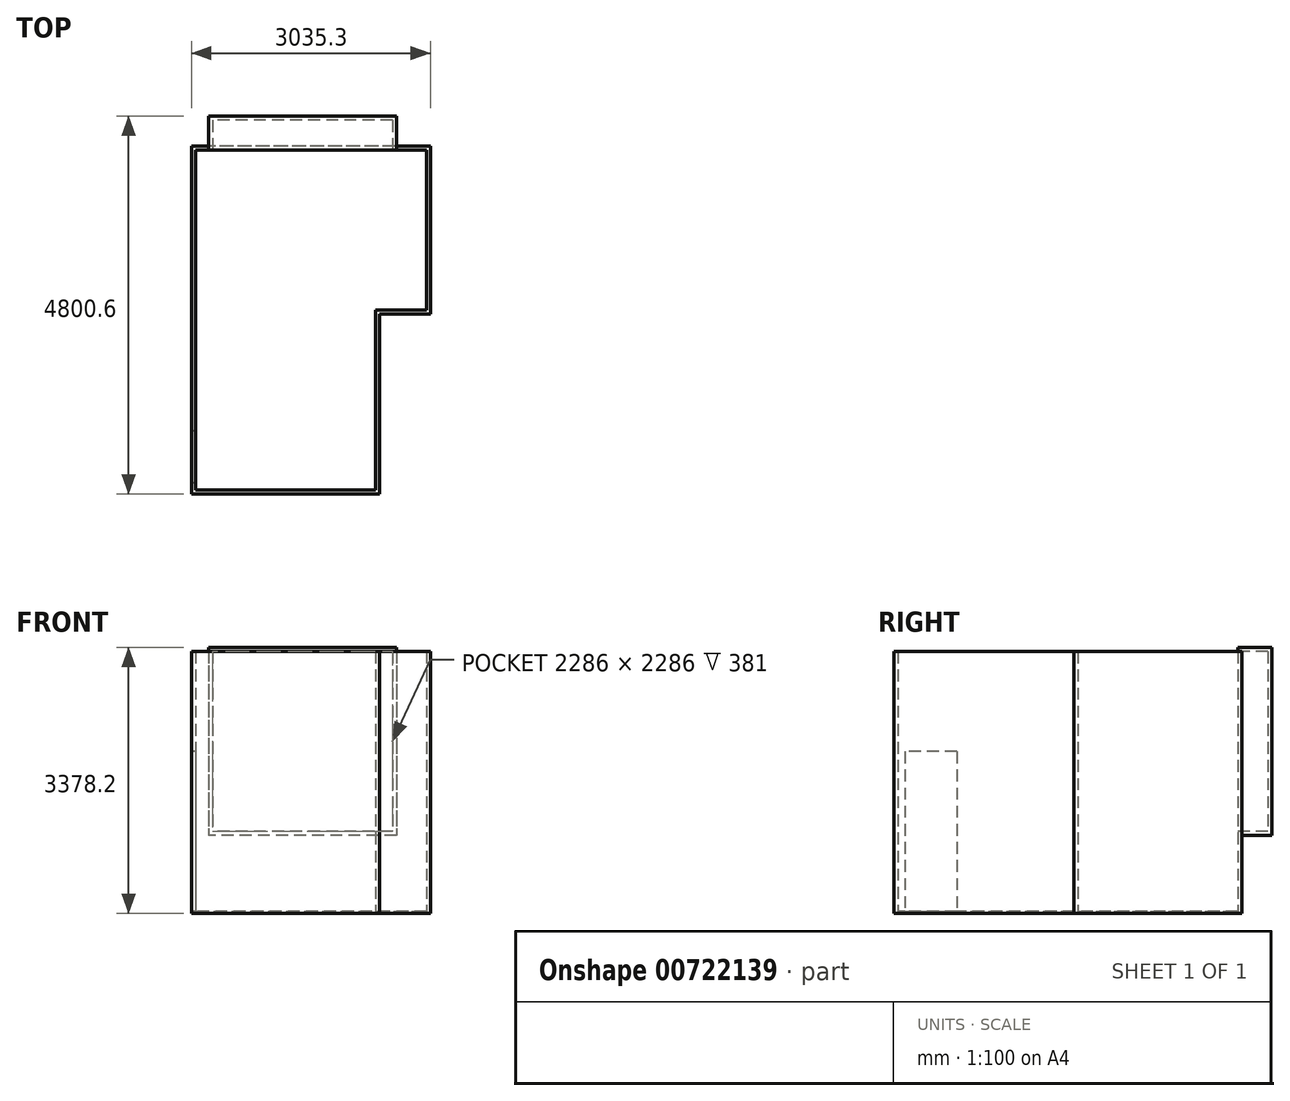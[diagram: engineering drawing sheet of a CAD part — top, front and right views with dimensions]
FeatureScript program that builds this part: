
annotation { "Feature Type Name" : "Feature", "Feature Type Description" : "" }
export const myFeature = defineFeature(function(context is Context, id is Id, definition is map)
    precondition{}
    {
        {
            var Q0;
            Q0=qCreatedBy(makeId("Top.planeOp"),FACE);
            var sketch = newSketch(context, id + "F0", { "sketchPlane" : qUnion([Q0])});
            skLineSegment(sketch, "E0", {"start": v(50.8, 4368.8) * mm, "end": v(50.8, 50.8) * mm});
            skLineSegment(sketch, "E1", {"start": v(50.8, 50.8) * mm, "end": v(2336.8, 50.8) * mm});
            skLineSegment(sketch, "E2", {"start": v(2336.8, 50.8) * mm, "end": v(2336.8, 2336.8) * mm});
            skLineSegment(sketch, "E3", {"start": v(2336.8, 2336.8) * mm, "end": v(2984.5, 2336.8) * mm});
            skLineSegment(sketch, "E4", {"start": v(2984.5, 2336.8) * mm, "end": v(2984.5, 4368.8) * mm});
            skLineSegment(sketch, "E5", {"start": v(2984.5, 4368.8) * mm, "end": v(50.8, 4368.8) * mm});
            skLineSegment(sketch, "E6", {"start": v(0, 4419.6) * mm, "end": v(0, 0) * mm});
            skLineSegment(sketch, "E7", {"start": v(0, 0) * mm, "end": v(2387.6, 0) * mm});
            skLineSegment(sketch, "E8", {"start": v(2387.6, 0) * mm, "end": v(2387.6, 2286) * mm});
            skLineSegment(sketch, "E9", {"start": v(2387.6, 2286) * mm, "end": v(3035.3, 2286) * mm});
            skLineSegment(sketch, "E10", {"start": v(3035.3, 2286) * mm, "end": v(3035.3, 4419.6) * mm});
            skLineSegment(sketch, "E11", {"start": v(3035.3, 4419.6) * mm, "end": v(0, 4419.6) * mm});
            skLineSegment(sketch, "E12", {"start": v(1193.8, 50.8) * mm, "end": v(1193.8, 0) * mm, "construction": true});
            skLineSegment(sketch, "E13", {"start": v(1517.65, 4368.8) * mm, "end": v(1517.65, 4419.6) * mm, "construction": true});
            skLineSegment(sketch, "E14", {"start": v(2984.5, 3352.8) * mm, "end": v(3035.3, 3352.8) * mm, "construction": true});
            skLineSegment(sketch, "E15", {"start": v(2336.8, 2286) * mm, "end": v(2387.6, 2286) * mm, "construction": true});
            skLineSegment(sketch, "E16", {"start": v(2362.2, 2336.8) * mm, "end": v(2362.2, 2286) * mm, "construction": true});
            skSolve(sketch);
        }
        {
            var Q0;
            Q0=makeQuery(id+"F0.imprint","IMPRINT",FACE,{"disambiguationData":[TD([[makeQuery(id+"F0.imprint","IMPRINT",EDGE,{"derivedFrom":sQuery(id+"F0.wireOp",EDGE,"E0")}),-1.0]])]});
            var sketch = newSketch(context, id + "F1", { "sketchPlane" : qUnion([Q0])});
            skLineSegment(sketch, "E17.top", {"start": v(0, 4419.6) * mm, "end": v(3035.3, 4419.6) * mm, "construction": true});
            skLineSegment(sketch, "E17.left", {"start": v(0, 0) * mm, "end": v(0, 4419.6) * mm});
            skLineSegment(sketch, "E18.bottom", {"start": v(0, 0) * mm, "end": v(2387.6, 0) * mm});
            skLineSegment(sketch, "E18.top", {"start": v(0, 4419.6) * mm, "end": v(3035.3, 4419.6) * mm});
            skLineSegment(sketch, "E19", {"start": v(3035.3, 4419.6) * mm, "end": v(3035.3, 2286) * mm});
            skLineSegment(sketch, "E20", {"start": v(3035.3, 2286) * mm, "end": v(2387.6, 2286) * mm});
            skLineSegment(sketch, "E21", {"start": v(2387.6, 2286) * mm, "end": v(2387.6, 0) * mm});
            skSolve(sketch);
        }
        {
            var Q0;
            Q0 = qSketchRegion(id + "F0", true);
            extrude(context, id + "F2", {"entities" : qUnion([Q0]), "depth" : 3302 * mm, "offsetDistance" : 25.4 * mm});
        }
        {
            var Q0;
            Q0 = qSketchRegion(id + "F1", true);
            extrude(context, id + "F3", {"entities" : qUnion([Q0]), "operationType" : NewBodyOperationType.ADD, "oppositeDirection" : true, "depth" : 25.4 * mm, "offsetDistance" : 25.4 * mm});
        }
        {
            var Q0;
            Q0=makeQuery(id+"F2.opExtrude","SWEPT_FACE",FACE,{"disambiguationData":[OSD([sQuery(id+"F0.wireOp",EDGE,"E6")])]});
            var sketch = newSketch(context, id + "F4", { "sketchPlane" : qUnion([Q0])});
            skLineSegment(sketch, "E22.bottom", {"start": v(-800.1, 2032) * mm, "end": v(-139.7, 2032) * mm});
            skLineSegment(sketch, "E22.top", {"start": v(-800.1, 0) * mm, "end": v(-139.7, 0) * mm});
            skLineSegment(sketch, "E22.left", {"start": v(-800.1, 2032) * mm, "end": v(-800.1, 0) * mm});
            skLineSegment(sketch, "E22.right", {"start": v(-139.7, 2032) * mm, "end": v(-139.7, 0) * mm});
            skLineSegment(sketch, "E23", {"start": v(-139.7, 2032) * mm, "end": v(0, 2032) * mm, "construction": true});
            skSolve(sketch);
        }
        {
            var Q0;
            Q0 = qSketchRegion(id + "F4", true);
            extrude(context, id + "F5", {"entities" : qUnion([Q0]), "operationType" : NewBodyOperationType.REMOVE, "endBound" : BoundingType.UP_TO_NEXT, "oppositeDirection" : true, "depth" : 25.4 * mm, "offsetDistance" : 25.4 * mm});
        }
        {
            var Q0;
            Q0=makeQuery(id+"F2.opExtrude","SWEPT_FACE",FACE,{"disambiguationData":[OSD([sQuery(id+"F0.wireOp",EDGE,"E5")])]});
            var sketch = newSketch(context, id + "F6", { "sketchPlane" : qUnion([Q0])});
            skLineSegment(sketch, "E24", {"start": v(1409.7, 0) * mm, "end": v(1409.7, 1016) * mm, "construction": true});
            skLineSegment(sketch, "E25.bottom", {"start": v(2552.7, 3302) * mm, "end": v(266.7, 3302) * mm, "construction": true});
            skLineSegment(sketch, "E25.top", {"start": v(2552.7, 1016) * mm, "end": v(266.7, 1016) * mm, "construction": true});
            skLineSegment(sketch, "E25.left", {"start": v(2552.7, 3302) * mm, "end": v(2552.7, 1016) * mm, "construction": true});
            skLineSegment(sketch, "E25.right", {"start": v(266.7, 3302) * mm, "end": v(266.7, 1016) * mm, "construction": true});
            skLineSegment(sketch, "E26", {"start": v(50.8, 2159) * mm, "end": v(266.7, 2159) * mm});
            skLineSegment(sketch, "E27.bottom", {"start": v(2603.5, 3352.8) * mm, "end": v(215.9, 3352.8) * mm});
            skLineSegment(sketch, "E27.top", {"start": v(2603.5, 965.2) * mm, "end": v(215.9, 965.2) * mm});
            skLineSegment(sketch, "E27.left", {"start": v(215.9, 3352.8) * mm, "end": v(215.9, 965.2) * mm});
            skLineSegment(sketch, "E27.right", {"start": v(2603.5, 3352.8) * mm, "end": v(2603.5, 965.2) * mm});
            skLineSegment(sketch, "E28", {"start": v(1409.7, 965.2) * mm, "end": v(1409.7, 1016) * mm, "construction": true});
            skLineSegment(sketch, "E29", {"start": v(2552.7, 2159) * mm, "end": v(2603.5, 2159) * mm, "construction": true});
            skSolve(sketch);
        }
        {
            var Q0;
            Q0 = qSketchRegion(id + "F6", true);
            extrude(context, id + "F7", {"entities" : qUnion([Q0]), "operationType" : NewBodyOperationType.ADD, "oppositeDirection" : true, "depth" : 431.8 * mm, "offsetDistance" : 25.4 * mm});
        }
        {
            var Q0;
            Q0=makeQuery(id+"F7.boolean.opBoolean","MERGE",FACE,{"derivedFrom":[makeQuery(id+"F2.opExtrude","SWEPT_FACE",FACE,{"disambiguationData":[OSD([sQuery(id+"F0.wireOp",EDGE,"E5")])]}),makeQuery(id+"F7.opExtrude","CAP_FACE",FACE,{"disambiguationData":[OSD([sQuery(id+"F6.wireOp",EDGE,"E27.bottom"),sQuery(id+"F6.wireOp",EDGE,"E27.top"),sQuery(id+"F6.wireOp",EDGE,"E27.left"),sQuery(id+"F6.wireOp",EDGE,"E27.right")])],"isStart":true})]});
            var sketch = newSketch(context, id + "F8", { "sketchPlane" : qUnion([Q0])});
            skLineSegment(sketch, "E30", {"start": v(1409.7, 0) * mm, "end": v(1409.7, 1016) * mm, "construction": true});
            skLineSegment(sketch, "E31.bottom", {"start": v(2552.7, 3302) * mm, "end": v(266.7, 3302) * mm});
            skLineSegment(sketch, "E31.top", {"start": v(2552.7, 1016) * mm, "end": v(266.7, 1016) * mm});
            skLineSegment(sketch, "E31.left", {"start": v(2552.7, 3302) * mm, "end": v(2552.7, 1016) * mm});
            skLineSegment(sketch, "E31.right", {"start": v(266.7, 3302) * mm, "end": v(266.7, 1016) * mm});
            skLineSegment(sketch, "E32", {"start": v(50.8, 2159) * mm, "end": v(266.7, 2159) * mm});
            skLineSegment(sketch, "E33.bottom", {"start": v(2603.5, 3352.8) * mm, "end": v(215.9, 3352.8) * mm, "construction": true});
            skLineSegment(sketch, "E33.top", {"start": v(2603.5, 965.2) * mm, "end": v(215.9, 965.2) * mm, "construction": true});
            skLineSegment(sketch, "E33.left", {"start": v(215.9, 3352.8) * mm, "end": v(215.9, 965.2) * mm, "construction": true});
            skLineSegment(sketch, "E33.right", {"start": v(2603.5, 3352.8) * mm, "end": v(2603.5, 965.2) * mm, "construction": true});
            skLineSegment(sketch, "E34", {"start": v(1409.7, 965.2) * mm, "end": v(1409.7, 1016) * mm, "construction": true});
            skLineSegment(sketch, "E35", {"start": v(2552.7, 2159) * mm, "end": v(2603.5, 2159) * mm, "construction": true});
            skSolve(sketch);
        }
        {
            var Q0;
            Q0 = qSketchRegion(id + "F8", true);
            extrude(context, id + "F9", {"entities" : qUnion([Q0]), "operationType" : NewBodyOperationType.REMOVE, "oppositeDirection" : true, "depth" : 381 * mm, "offsetDistance" : 25.4 * mm});
        }
    });
